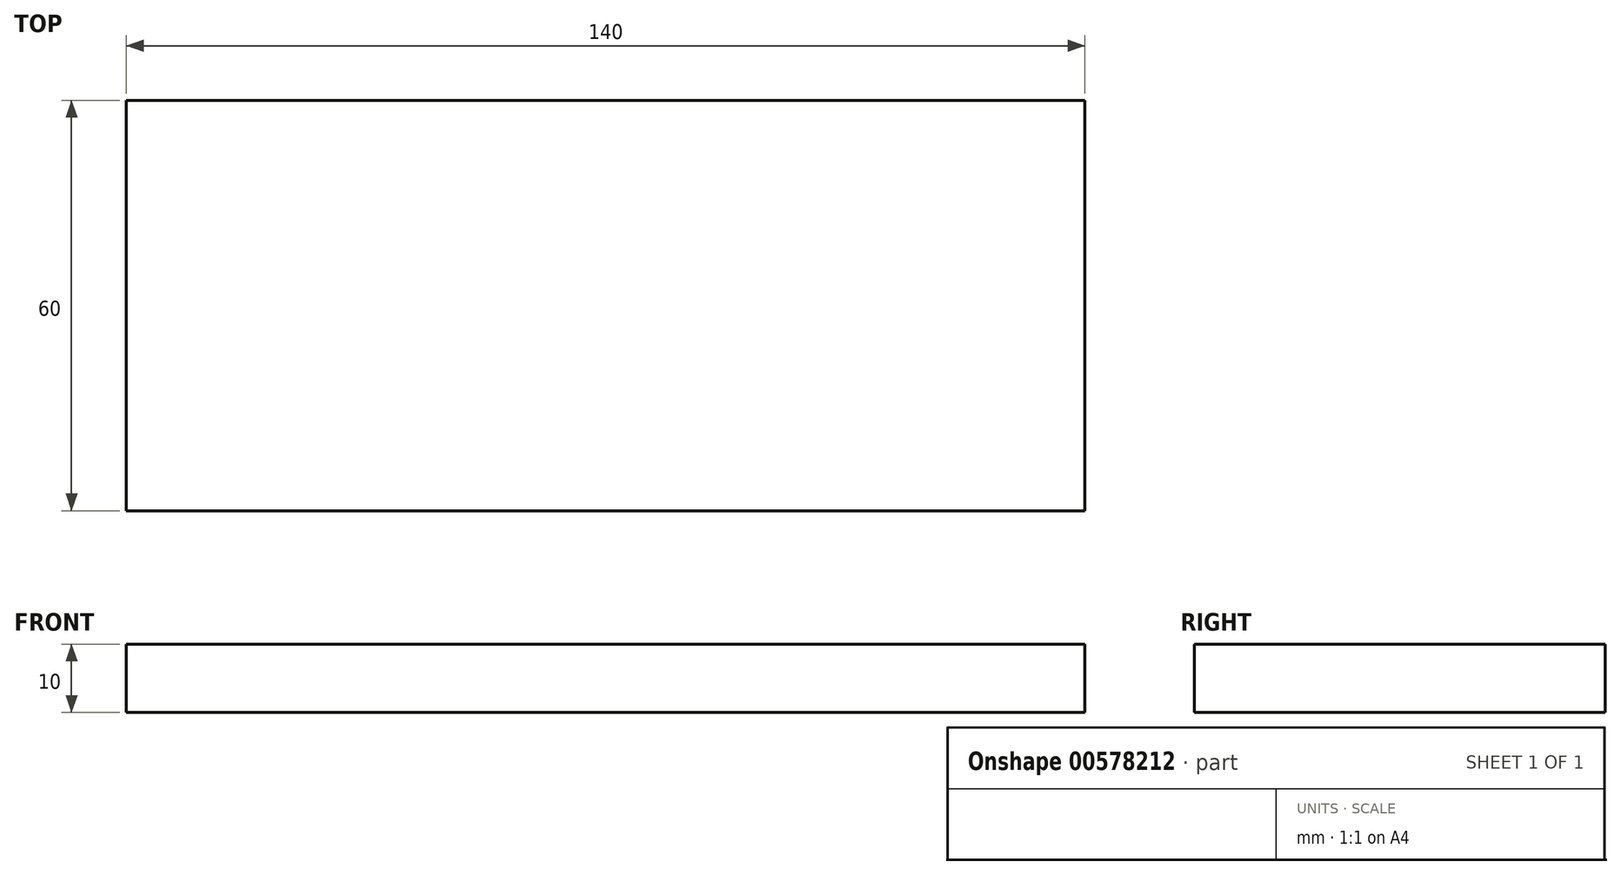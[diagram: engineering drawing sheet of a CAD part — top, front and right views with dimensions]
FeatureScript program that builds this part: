
annotation { "Feature Type Name" : "Feature", "Feature Type Description" : "" }
export const myFeature = defineFeature(function(context is Context, id is Id, definition is map)
    precondition{}
    {
        {
            var Q0;
            Q0=qCreatedBy(makeId("Top.planeOp"),FACE);
            var sketch = newSketch(context, id + "F0", { "sketchPlane" : qUnion([Q0])});
            skLineSegment(sketch, "E0.bottom", {"start": v(70, -30) * mm, "end": v(-70, -30) * mm});
            skLineSegment(sketch, "E0.top", {"start": v(70, 30) * mm, "end": v(-70, 30) * mm});
            skLineSegment(sketch, "E0.left", {"start": v(70, -30) * mm, "end": v(70, 30) * mm});
            skLineSegment(sketch, "E0.right", {"start": v(-70, -30) * mm, "end": v(-70, 30) * mm});
            skPoint(sketch, "E0.middle", {"position": v(0, 0) * mm});
            skSolve(sketch);
        }
        {
            var Q0;
            Q0=qSketchRegion(id+"F0",true);
            extrude(context, id + "F1", {"entities" : qUnion([Q0]), "endBound" : BoundingType.SYMMETRIC, "depth" : 10 * mm, "offsetDistance" : 25 * mm});
        }
    });
